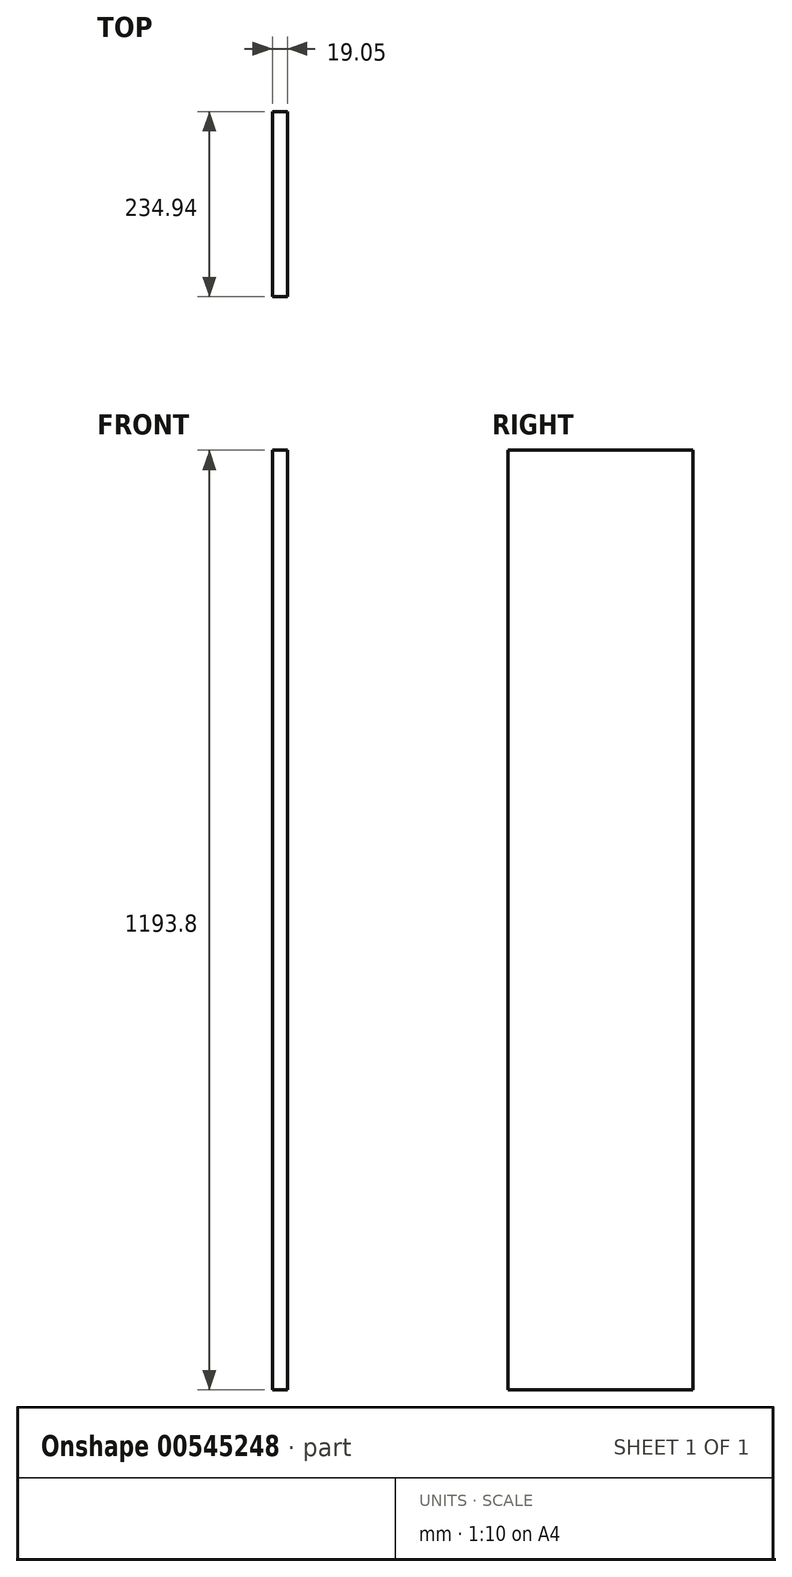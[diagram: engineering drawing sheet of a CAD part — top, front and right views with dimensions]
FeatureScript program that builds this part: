
annotation { "Feature Type Name" : "Feature", "Feature Type Description" : "" }
export const myFeature = defineFeature(function(context is Context, id is Id, definition is map)
    precondition{}
    {
        {
            var Q0;
            Q0=qCreatedBy(makeId("Right.planeOp"),FACE);
            cPlane(context, id + "F0", {"entities" : qUnion([Q0]), "cplaneType" : CPlaneType.OFFSET, "offset" : 584.2 * mm, "width" : 152.4 * mm, "height" : 152.4 * mm});
        }
        {
            var Q0;
            Q0=qCreatedBy(id+"F0.planeOp",FACE);
            var sketch = newSketch(context, id + "F1", { "sketchPlane" : qUnion([Q0])});
            skLineSegment(sketch, "E0.bottom", {"start": v(117.47, 596.9) * mm, "end": v(-117.48, 596.9) * mm});
            skLineSegment(sketch, "E0.top", {"start": v(117.48, -596.9) * mm, "end": v(-117.47, -596.9) * mm});
            skLineSegment(sketch, "E0.left", {"start": v(117.47, 596.9) * mm, "end": v(117.48, -596.9) * mm});
            skLineSegment(sketch, "E0.right", {"start": v(-117.48, 596.9) * mm, "end": v(-117.47, -596.9) * mm});
            skPoint(sketch, "E0.middle", {"position": v(0, 0) * mm});
            skSolve(sketch);
        }
        {
            var Q0;
            Q0=makeQuery(id+"F1.imprint","IMPRINT",FACE,{"disambiguationData":[TD([[makeQuery(id+"F1.imprint","IMPRINT",EDGE,{"derivedFrom":sQuery(id+"F1.wireOp",EDGE,"E0.bottom")}),1.0]])]});
            extrude(context, id + "F2", {"entities" : qUnion([Q0]), "depth" : 19.05 * mm, "offsetDistance" : 25.4 * mm});
        }
    });
